# Revit family: 306_R3_-_-S_
name_source: partatom
category: Pipe Accessories
units: mm (PartAtom-declared; Revit-internal decimal feet)

## family parameters
Always vertical = Yes
Cut with Voids When Loaded = No
Part Type = Valve - Breaks Into
Round Connector Dimension = Use Diameter
Shared = No
Work Plane-Based = No

## types (17) — shared parameters
B33 = 4 mm  [stored 0.0131234 ft]
B4 = 11 mm
BB = 23 mm
CAT0 = Yes
Description = Change-over ball valve, 3-way, Internal thread
FD1 = 23 mm
FD4 = 11 mm
H2 = 8 mm  [stored 0.0262467 ft]
L2D_Min = 3048 mm
Manufacturer = Belimo
QmdConnectorList = 301;D;302;D;303;D
magiPartTypeId = 306
magiProductFamilyId = R3*-*-S*
zero-valued in all types: MC_Default_elevation

## per-type parameters (varying)
| type | CenSd_D11_6 | D | D11 | D33 | FD | H | H1 | H11 | H1__ve | L1 | L2 | L2D | L3 | LL | M | M__ve | W2D |
| R3015-P25-S1 | 9 mm  [stored 0.0295276 ft] | 15 mm | 11 mm | 10 mm  [stored 0.0328084 ft] | 26 mm | 35 mm | 4 mm  [stored 0.0131234 ft] | 31 mm | -4 mm | 18 mm  [stored 0.0590551 ft] | 35 mm | 67 mm | 15 mm  [stored 0.0492126 ft] | 34 mm  [stored 0.111549 ft] | 36 mm | -36 mm  [stored -0.11811 ft] | 15 mm  [stored 0.0492126 ft] |
| R3050-58-S4 | 30 mm  [stored 0.0984252 ft] | 50 mm | 35 mm | 27 mm  [stored 0.0885827 ft] | 85 mm | 68 mm | 9 mm  [stored 0.0295276 ft] | 60 mm | -9 mm | 38 mm | 73 mm | 142 mm | 31 mm | 71 mm | 79 mm | -79 mm  [stored -0.259186 ft] | 50 mm |
| R3050-40-S4 | 30 mm  [stored 0.0984252 ft] | 50 mm | 35 mm | 27 mm  [stored 0.0885827 ft] | 85 mm | 68 mm | 9 mm  [stored 0.0295276 ft] | 60 mm | -9 mm | 38 mm | 73 mm | 142 mm | 31 mm | 71 mm | 79 mm | -79 mm  [stored -0.259186 ft] | 50 mm |
| R3050-25-S4 | 30 mm  [stored 0.0984252 ft] | 50 mm | 35 mm | 27 mm  [stored 0.0885827 ft] | 85 mm | 56 mm | 7 mm  [stored 0.0229659 ft] | 49 mm | -7 mm  [stored -0.0229659 ft] | 33 mm | 65 mm | 125 mm | 27 mm  [stored 0.0885827 ft] | 63 mm | 68 mm | -68 mm  [stored -0.223097 ft] | 50 mm |
| R3040-25-S4 | 24 mm | 40 mm | 28 mm  [stored 0.0918635 ft] | 22 mm  [stored 0.0721785 ft] | 68 mm | 62 mm | 8 mm  [stored 0.0262467 ft] | 54 mm | -8 mm | 33 mm | 63 mm | 122 mm | 26 mm | 61 mm | 67 mm | -67 mm | 40 mm |
| R3040-16-S3 | 24 mm | 40 mm | 28 mm  [stored 0.0918635 ft] | 22 mm  [stored 0.0721785 ft] | 68 mm | 51 mm | 6 mm  [stored 0.019685 ft] | 44 mm | -6 mm | 30 mm  [stored 0.0984252 ft] | 57 mm | 111 mm | 24 mm | 56 mm | 56 mm | -56 mm  [stored -0.183727 ft] | 40 mm |
| R3032-16-S3 | 19 mm | 32 mm | 22 mm  [stored 0.0721785 ft] | 18 mm  [stored 0.0590551 ft] | 54 mm | 51 mm | 6 mm  [stored 0.019685 ft] | 44 mm | -6 mm | 28 mm  [stored 0.0918635 ft] | 54 mm | 105 mm | 23 mm | 53 mm | 56 mm | -56 mm  [stored -0.183727 ft] | 32 mm  [stored 0.104987 ft] |
| R3025-10-S2 | 15 mm  [stored 0.0492126 ft] | 25 mm | 18 mm  [stored 0.0590551 ft] | 15 mm  [stored 0.0492126 ft] | 43 mm | 46 mm | 6 mm  [stored 0.019685 ft] | 40 mm | -6 mm | 23 mm | 45 mm | 87 mm | 19 mm | 44 mm | 45 mm | -45 mm  [stored -0.147638 ft] | 25 mm  [stored 0.082021 ft] |
| R3025-6P3-S2 | 15 mm  [stored 0.0492126 ft] | 25 mm | 18 mm  [stored 0.0590551 ft] | 15 mm  [stored 0.0492126 ft] | 43 mm | 46 mm | 6 mm  [stored 0.019685 ft] | 40 mm | -6 mm | 23 mm | 45 mm | 87 mm | 19 mm | 44 mm | 45 mm | -45 mm  [stored -0.147638 ft] | 25 mm  [stored 0.082021 ft] |
| R3020-6P3-S2 | 12 mm  [stored 0.0393701 ft] | 20 mm | 14 mm  [stored 0.0459318 ft] | 12 mm  [stored 0.0393701 ft] | 34 mm  [stored 0.111549 ft] | 46 mm | 6 mm  [stored 0.019685 ft] | 40 mm | -6 mm | 21 mm | 40 mm | 78 mm | 17 mm | 39 mm | 42 mm | -42 mm | 20 mm  [stored 0.0656168 ft] |
| R3020-4-S2 | 12 mm  [stored 0.0393701 ft] | 20 mm | 14 mm  [stored 0.0459318 ft] | 12 mm  [stored 0.0393701 ft] | 34 mm  [stored 0.111549 ft] | 46 mm | 6 mm  [stored 0.019685 ft] | 40 mm | -6 mm | 21 mm | 40 mm | 78 mm | 17 mm | 39 mm | 42 mm | -42 mm | 20 mm  [stored 0.0656168 ft] |
| R3015-4-S1 | 9 mm  [stored 0.0295276 ft] | 15 mm | 11 mm | 10 mm  [stored 0.0328084 ft] | 26 mm | 44 mm | 6 mm  [stored 0.019685 ft] | 39 mm | -6 mm | 18 mm  [stored 0.0590551 ft] | 35 mm | 67 mm | 15 mm  [stored 0.0492126 ft] | 34 mm  [stored 0.111549 ft] | 36 mm | -36 mm  [stored -0.11811 ft] | 15 mm  [stored 0.0492126 ft] |
| R3015-2P5-S1 | 9 mm  [stored 0.0295276 ft] | 15 mm | 11 mm | 10 mm  [stored 0.0328084 ft] | 26 mm | 44 mm | 6 mm  [stored 0.019685 ft] | 39 mm | -6 mm | 18 mm  [stored 0.0590551 ft] | 35 mm | 67 mm | 15 mm  [stored 0.0492126 ft] | 34 mm  [stored 0.111549 ft] | 36 mm | -36 mm  [stored -0.11811 ft] | 15 mm  [stored 0.0492126 ft] |
| R3015-1P6-S1 | 9 mm  [stored 0.0295276 ft] | 15 mm | 11 mm | 10 mm  [stored 0.0328084 ft] | 26 mm | 44 mm | 6 mm  [stored 0.019685 ft] | 39 mm | -6 mm | 18 mm  [stored 0.0590551 ft] | 35 mm | 67 mm | 15 mm  [stored 0.0492126 ft] | 34 mm  [stored 0.111549 ft] | 36 mm | -36 mm  [stored -0.11811 ft] | 15 mm  [stored 0.0492126 ft] |
| R3015-1-S1 | 9 mm  [stored 0.0295276 ft] | 15 mm | 11 mm | 10 mm  [stored 0.0328084 ft] | 26 mm | 35 mm | 4 mm  [stored 0.0131234 ft] | 31 mm | -4 mm | 18 mm  [stored 0.0590551 ft] | 35 mm | 67 mm | 15 mm  [stored 0.0492126 ft] | 34 mm  [stored 0.111549 ft] | 36 mm | -36 mm  [stored -0.11811 ft] | 15 mm  [stored 0.0492126 ft] |
| R3015-P63-S1 | 9 mm  [stored 0.0295276 ft] | 15 mm | 11 mm | 10 mm  [stored 0.0328084 ft] | 26 mm | 35 mm | 4 mm  [stored 0.0131234 ft] | 31 mm | -4 mm | 18 mm  [stored 0.0590551 ft] | 35 mm | 67 mm | 15 mm  [stored 0.0492126 ft] | 34 mm  [stored 0.111549 ft] | 36 mm | -36 mm  [stored -0.11811 ft] | 15 mm  [stored 0.0492126 ft] |
| R3015-P4-S1 | 9 mm  [stored 0.0295276 ft] | 15 mm | 11 mm | 10 mm  [stored 0.0328084 ft] | 26 mm | 35 mm | 4 mm  [stored 0.0131234 ft] | 31 mm | -4 mm | 18 mm  [stored 0.0590551 ft] | 35 mm | 67 mm | 15 mm  [stored 0.0492126 ft] | 34 mm  [stored 0.111549 ft] | 36 mm | -36 mm  [stored -0.11811 ft] | 15 mm  [stored 0.0492126 ft] |

note: column(s) folded — value = type name in every type: magiProductCode, magiProductId

note: [stored X ft] marks values corroborated as IEEE doubles in the binary element streams (Revit-internal decimal feet)

## geometry (parser evidence)
native form markers: Sweep x1
no freeform markers — native parametric forms only
